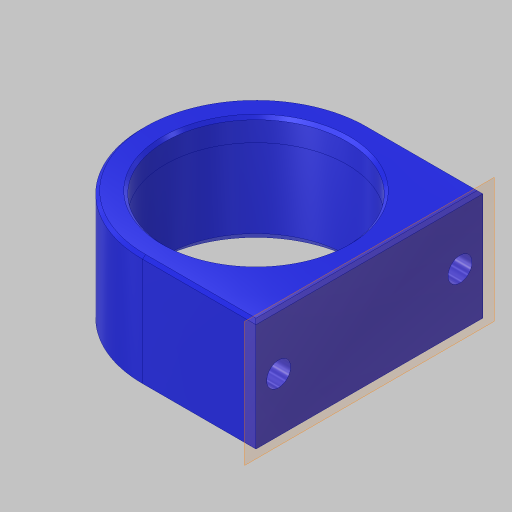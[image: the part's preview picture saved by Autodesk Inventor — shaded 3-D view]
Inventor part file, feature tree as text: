
AUTODESK INVENTOR PART (.ipt)
format: ipt  version: 2023.5 (Build 275446000, 446)  size: 179,200 bytes
history: native  units: in
note: dims shown in document units (in); Inventor stores cm internally (conversion verified against a paired STEP export)
features: extrude x3, sketch x3, chamfer x2, plane x1
ambient origin geometry x8: Origin, YZ Plane, XZ Plane, XY Plane, X Axis, Y Axis, Z Axis, Center Point
bodies: Solid1 (feature_tree)
feature tree (9):
  extrude  "Extrusion1"  Depth=2.5in
  extrude  "Extrusion2"  Depth=1.0in
  chamfer  "Chamfer1"  Distance=1.0in
  plane  "Work Plane1"
  extrude  "Extrusion4"  Depth=2.5in
  chamfer  "Chamfer3"  Distance=2.0in
  sketch  "Sketch1"  dims[d0=2.0in d1=2.5in]
  sketch  "Sketch2"  dims[d2=0.25in d3=0.0in d4=2.02in d5=1.0in d6=0.0in]
  sketch  "Sketch5"  dims[d21=0.125in d22=0.125in d23=45.0deg d27=2.5in d28=2.0in d29=0.2638in d30=1.0in d31=0.0in d32=0.0312in d33=0.125in d34=45.0deg]
